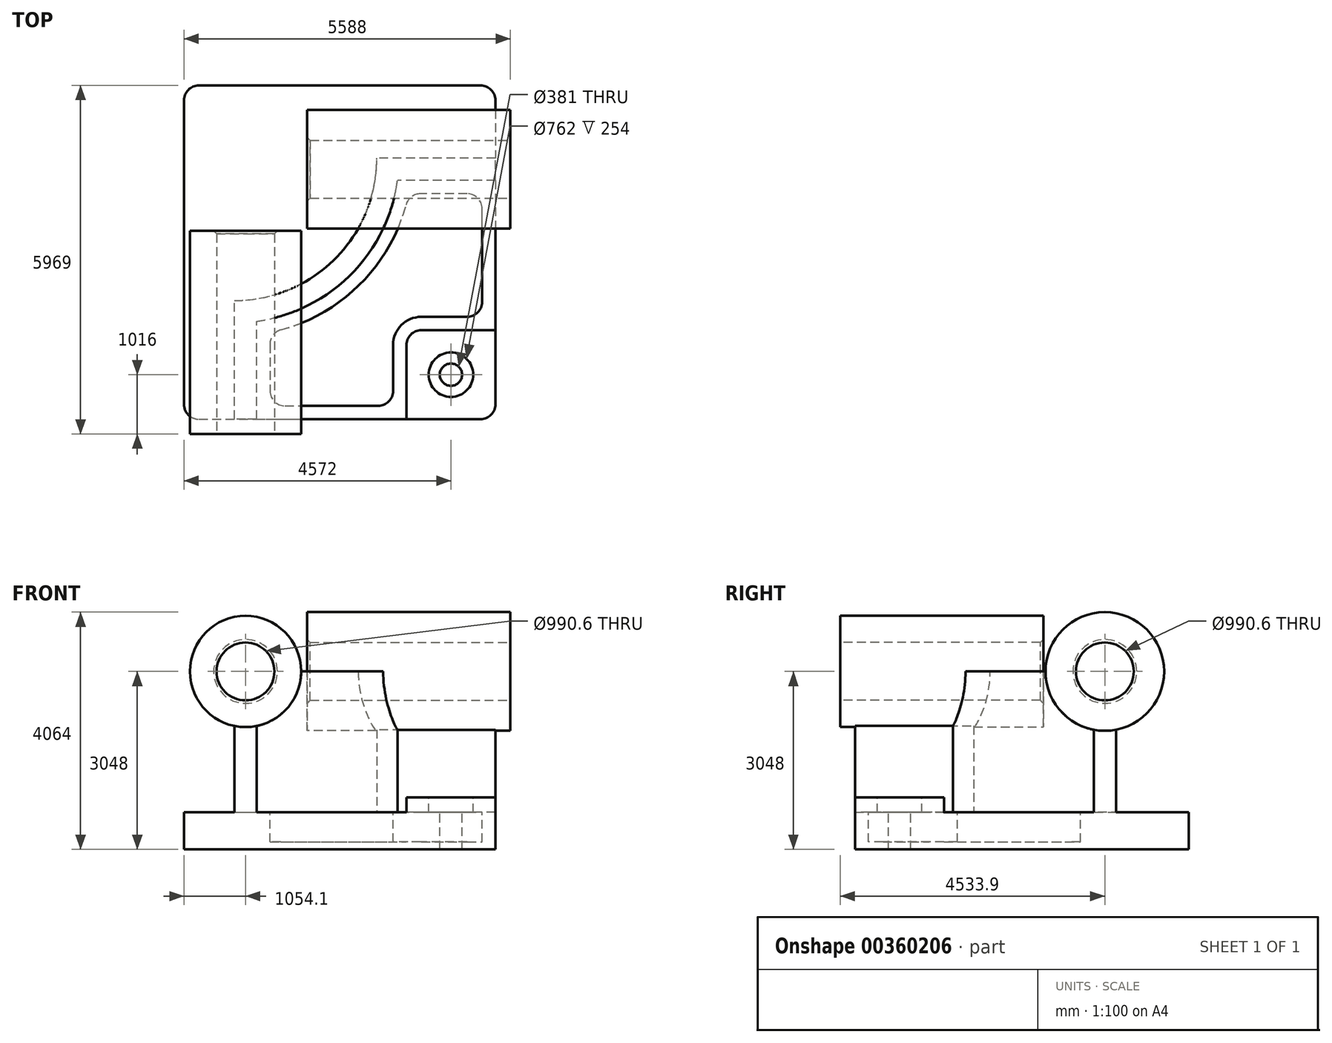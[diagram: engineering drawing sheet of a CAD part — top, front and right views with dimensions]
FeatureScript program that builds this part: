
annotation { "Feature Type Name" : "Feature", "Feature Type Description" : "" }
export const myFeature = defineFeature(function(context is Context, id is Id, definition is map)
    precondition{}
    {
        {
            var Q0;
            Q0=qCreatedBy(makeId("Top.planeOp"),FACE);
            var sketch = newSketch(context, id + "F0", { "sketchPlane" : qUnion([Q0])});
            skLineSegment(sketch, "E0.bottom", {"start": v(-2667, 2857.5) * mm, "end": v(2667, 2857.5) * mm});
            skLineSegment(sketch, "E0.top", {"start": v(-2667, -2857.5) * mm, "end": v(2667, -2857.5) * mm});
            skLineSegment(sketch, "E0.left", {"start": v(-2667, 2857.5) * mm, "end": v(-2667, -2857.5) * mm});
            skLineSegment(sketch, "E0.right", {"start": v(2667, 2857.5) * mm, "end": v(2667, -2857.5) * mm});
            skPoint(sketch, "E0.middle", {"position": v(0, 0) * mm});
            skSolve(sketch);
        }
        {
            var Q0;
            Q0=makeQuery(id+"F0.imprint","IMPRINT",FACE,{"disambiguationData":[TD([[makeQuery(id+"F0.imprint","IMPRINT",EDGE,{"derivedFrom":sQuery(id+"F0.wireOp",EDGE,"E0.bottom")}),-1.0]])]});
            extrude(context, id + "F1", {"entities" : qUnion([Q0]), "depth" : 635 * mm});
        }
        {
            var Q0;
            Q0=makeQuery(id+"F1.opExtrude","CAP_FACE",FACE,{"disambiguationData":[OSD([sQuery(id+"F0.wireOp",EDGE,"E0.bottom"),sQuery(id+"F0.wireOp",EDGE,"E0.top"),sQuery(id+"F0.wireOp",EDGE,"E0.left"),sQuery(id+"F0.wireOp",EDGE,"E0.right")])],"isStart":false});
            var sketch = newSketch(context, id + "F2", { "sketchPlane" : qUnion([Q0])});
            skLineSegment(sketch, "E1", {"start": v(-1803.4, -2857.5) * mm, "end": v(-1803.4, -825.5) * mm});
            skLineSegment(sketch, "E2", {"start": v(2667, 1612.9) * mm, "end": v(635, 1612.9) * mm});
            skArc(sketch, "E3", {"start": v(-1803.4, -825.5) * mm, "mid": v(-79.2, -111.3) * mm, "end": v(635, 1612.9) * mm});
            skLineSegment(sketch, "E4", {"start": v(-1803.4, 1612.9) * mm, "end": v(635, 1612.9) * mm, "construction": true});
            skLineSegment(sketch, "E5", {"start": v(-1803.4, 1612.9) * mm, "end": v(-1803.4, -825.5) * mm, "construction": true});
            skLineSegment(sketch, "E6.0", {"start": v(-1422.4, -2857.5) * mm, "end": v(-1422.4, -1180.64) * mm});
            skArc(sketch, "E6.1", {"start": v(-1422.4, -1180.64) * mm, "mid": v(190.22, -380.72) * mm, "end": v(990.14, 1231.9) * mm});
            skLineSegment(sketch, "E6.2", {"start": v(2667, 1231.9) * mm, "end": v(990.14, 1231.9) * mm});
            skLineSegment(sketch, "E7.0", {"start": v(2667, 2857.5) * mm, "end": v(2667, -2857.5) * mm});
            skLineSegment(sketch, "E8.0", {"start": v(-2667, -2857.5) * mm, "end": v(2667, -2857.5) * mm});
            skSolve(sketch);
        }
        {
            var Q0;
            {var subQ2=sQuery(id+"F2.wireOp",EDGE,"E1");Q0=makeQuery(id+"F2.imprint","IMPRINT",FACE,{"disambiguationData":[TD([[makeQuery(id+"F2.imprint","IMPRINT",EDGE,{"derivedFrom":subQ2}),-1.0]])]});}
            extrude(context, id + "F3", {"entities" : qUnion([Q0]), "operationType" : NewBodyOperationType.ADD, "depth" : 2413 * mm});
        }
        {
            var Q0;
            Q0=makeQuery(id+"F3.boolean.opBoolean","MERGE",FACE,{"derivedFrom":[makeQuery(id+"F1.opExtrude","SWEPT_FACE",FACE,{"disambiguationData":[OSD([sQuery(id+"F0.wireOp",EDGE,"E0.top")])]}),makeQuery(id+"F3.opExtrude","SWEPT_FACE",FACE,{"disambiguationData":[OSD([sQuery(id+"F2.wireOp",EDGE,"E8.0")])]})]});
            var sketch = newSketch(context, id + "F4", { "sketchPlane" : qUnion([Q0])});
            skCircle(sketch, "E9", {"center": v(-1612.9, 3048) * mm, "radius": 952.5 * mm});
            skSolve(sketch);
        }
        {
            var Q0;
            Q0 = qSketchRegion(id + "F4", true);
            extrude(context, id + "F5", {"entities" : qUnion([Q0]), "operationType" : NewBodyOperationType.ADD, "depth" : 254 * mm, "hasSecondDirection" : true, "secondDirectionOppositeDirection" : true, "secondDirectionDepth" : 3225.8 * mm});
        }
        {
            var Q0;
            Q0=makeQuery(id+"F3.boolean.opBoolean","MERGE",FACE,{"derivedFrom":[makeQuery(id+"F1.opExtrude","SWEPT_FACE",FACE,{"disambiguationData":[OSD([sQuery(id+"F0.wireOp",EDGE,"E0.right")])]}),makeQuery(id+"F3.opExtrude","SWEPT_FACE",FACE,{"disambiguationData":[OSD([sQuery(id+"F2.wireOp",EDGE,"E7.0")])]})]});
            var sketch = newSketch(context, id + "F6", { "sketchPlane" : qUnion([Q0])});
            skCircle(sketch, "E10", {"center": v(1422.4, 3048) * mm, "radius": 1016 * mm});
            skSolve(sketch);
        }
        {
            var Q0;
            Q0 = qSketchRegion(id + "F6", true);
            extrude(context, id + "F7", {"entities" : qUnion([Q0]), "operationType" : NewBodyOperationType.ADD, "depth" : 254 * mm, "hasSecondDirection" : true, "secondDirectionOppositeDirection" : true, "secondDirectionDepth" : 3225.8 * mm});
        }
        {
            var Q0;
            {var subQ0=sQuery(id+"F0.wireOp",EDGE,"E0.right");var subQ1=sQuery(id+"F0.wireOp",EDGE,"E0.top");Q0=makeQuery(id+"F3.boolean.opBoolean","SPLIT",FACE,{"disambiguationData":[TD([makeQuery(id+"F3.opExtrude","SWEPT_FACE",FACE,{"disambiguationData":[OSD([sQuery(id+"F2.wireOp",EDGE,"E6.0")])]})])],"derivedFrom":makeQuery(id+"F1.opExtrude","CAP_FACE",FACE,{"disambiguationData":[OSD([sQuery(id+"F0.wireOp",EDGE,"E0.bottom"),subQ1,sQuery(id+"F0.wireOp",EDGE,"E0.left"),subQ0])],"isStart":false})});}
            var sketch = newSketch(context, id + "F8", { "sketchPlane" : qUnion([Q0])});
            skLineSegment(sketch, "E11.bottom", {"start": v(2667, -2857.5) * mm, "end": v(1143, -2857.5) * mm});
            skLineSegment(sketch, "E11.top", {"start": v(2667, -1333.5) * mm, "end": v(1143, -1333.5) * mm});
            skLineSegment(sketch, "E11.left", {"start": v(2667, -2857.5) * mm, "end": v(2667, -1333.5) * mm});
            skLineSegment(sketch, "E11.right", {"start": v(1143, -2857.5) * mm, "end": v(1143, -1333.5) * mm});
            skSolve(sketch);
        }
        {
            var Q0;
            Q0=makeQuery(id+"F8.imprint","IMPRINT",FACE,{"disambiguationData":[TD([[makeQuery(id+"F8.imprint","IMPRINT",EDGE,{"derivedFrom":sQuery(id+"F8.wireOp",EDGE,"E11.bottom")}),1.0]])]});
            extrude(context, id + "F9", {"entities" : qUnion([Q0]), "operationType" : NewBodyOperationType.ADD, "depth" : 254 * mm});
        }
        {
            var Q0;
            Q0=makeQuery(id+"F9.opExtrude","SWEPT_EDGE",EDGE,{"disambiguationData":[OSD([sQuery(id+"F8.wireOp",EDGE,"E11.top"),sQuery(id+"F8.wireOp",EDGE,"E11.right")])]});
            fillet(context, id + "F10", {"entities" : qUnion([Q0]), "radius" : 254 * mm, "tangentPropagation" : true, "allowEdgeOverflow" : false});
        }
        {
            var Q0;
            {var subQ0=sQuery(id+"F0.wireOp",EDGE,"E0.right");var subQ1=sQuery(id+"F0.wireOp",EDGE,"E0.top");Q0=makeQuery(id+"F3.boolean.opBoolean","SPLIT",FACE,{"disambiguationData":[TD([makeQuery(id+"F3.opExtrude","SWEPT_FACE",FACE,{"disambiguationData":[OSD([sQuery(id+"F2.wireOp",EDGE,"E6.0")])]})])],"derivedFrom":makeQuery(id+"F1.opExtrude","CAP_FACE",FACE,{"disambiguationData":[OSD([sQuery(id+"F0.wireOp",EDGE,"E0.bottom"),subQ1,sQuery(id+"F0.wireOp",EDGE,"E0.left"),subQ0])],"isStart":false})});}
            var sketch = newSketch(context, id + "F11", { "sketchPlane" : qUnion([Q0])});
            skLineSegment(sketch, "E12.0", {"start": v(-1193.8, -1373.52) * mm, "end": v(-1193.8, -2628.9) * mm});
            skArc(sketch, "E12.1", {"start": v(1183.02, 1003.3) * mm, "mid": v(351.86, -542.36) * mm, "end": v(-1193.8, -1373.52) * mm});
            skLineSegment(sketch, "E12.2", {"start": v(-1193.8, -2628.9) * mm, "end": v(914.4, -2628.9) * mm});
            skLineSegment(sketch, "E12.3", {"start": v(2438.4, 1003.3) * mm, "end": v(1183.02, 1003.3) * mm});
            skLineSegment(sketch, "E12.4", {"start": v(914.4, -2628.9) * mm, "end": v(914.4, -1587.5) * mm});
            skArc(sketch, "E12.5", {"start": v(914.4, -1587.5) * mm, "mid": v(1055.75, -1246.25) * mm, "end": v(1397, -1104.9) * mm});
            skLineSegment(sketch, "E12.6", {"start": v(1397, -1104.9) * mm, "end": v(2438.4, -1104.9) * mm});
            skLineSegment(sketch, "E12.7", {"start": v(2438.4, -1104.9) * mm, "end": v(2438.4, 1003.3) * mm});
            skLineSegment(sketch, "E13.0", {"start": v(-1428.75, -1175.09) * mm, "end": v(-1428.75, -2863.85) * mm});
            skArc(sketch, "E13.1", {"start": v(984.59, 1238.25) * mm, "mid": v(185.73, -376.23) * mm, "end": v(-1428.75, -1175.09) * mm});
            skLineSegment(sketch, "E13.2", {"start": v(-1428.75, -2863.85) * mm, "end": v(1149.35, -2863.85) * mm});
            skLineSegment(sketch, "E13.3", {"start": v(2673.35, 1238.25) * mm, "end": v(984.59, 1238.25) * mm});
            skLineSegment(sketch, "E13.4", {"start": v(1149.35, -2863.85) * mm, "end": v(1149.35, -1587.5) * mm});
            skArc(sketch, "E13.5", {"start": v(1149.35, -1587.5) * mm, "mid": v(1221.89, -1412.39) * mm, "end": v(1397, -1339.85) * mm});
            skLineSegment(sketch, "E13.6", {"start": v(1397, -1339.85) * mm, "end": v(2673.35, -1339.85) * mm});
            skLineSegment(sketch, "E13.7", {"start": v(2673.35, -1339.85) * mm, "end": v(2673.35, 1238.25) * mm});
            skSolve(sketch);
        }
        {
            var Q0;
            Q0=makeQuery(id+"F11.imprint","IMPRINT",FACE,{"disambiguationData":[TD([[makeQuery(id+"F11.imprint","IMPRINT",EDGE,{"derivedFrom":sQuery(id+"F11.wireOp",EDGE,"E12.0")}),1.0]])]});
            extrude(context, id + "F12", {"entities" : qUnion([Q0]), "operationType" : NewBodyOperationType.REMOVE, "oppositeDirection" : true, "depth" : 508 * mm});
        }
        {
            var Q0;
            Q0=makeQuery(id+"F9.opExtrude","CAP_FACE",FACE,{"disambiguationData":[OSD([sQuery(id+"F8.wireOp",EDGE,"E11.bottom"),sQuery(id+"F8.wireOp",EDGE,"E11.top"),sQuery(id+"F8.wireOp",EDGE,"E11.left"),sQuery(id+"F8.wireOp",EDGE,"E11.right")])],"isStart":false});
            var sketch = newSketch(context, id + "F13", { "sketchPlane" : qUnion([Q0])});
            skCircle(sketch, "E14", {"center": v(1905, -2095.5) * mm, "radius": 381 * mm});
            skSolve(sketch);
        }
        {
            var Q0;
            Q0=sQuery(id+"F13.wireOp",VERTEX,"E14.center");
            var Q1;
            Q1=makeQuery(id+"F1.opExtrude","SWEPT_BODY",BODY,{"disambiguationData":[OSD([sQuery(id+"F0.wireOp",EDGE,"E0.bottom"),sQuery(id+"F0.wireOp",EDGE,"E0.top"),sQuery(id+"F0.wireOp",EDGE,"E0.left"),sQuery(id+"F0.wireOp",EDGE,"E0.right")])]});
            hole(context, id + "F14", {"style" : HoleStyle.C_BORE, "endStyle" : HoleEndStyle.THROUGH, "holeDiameter" : 381 * mm, "cBoreDiameter" : 762 * mm, "cBoreDepth" : 254 * mm, "isTappedThrough" : true, "tappedDepth" : 12.7 * mm, "tapClearance" : 3, "locations" : qUnion([Q0]), "scope" : qUnion([Q1])});
        }
        {
            var Q0;
            Q0=makeQuery(id+"F12.boolean.opBoolean","COPY",EDGE,{"derivedFrom":makeQuery(id+"F12.opExtrude","SWEPT_EDGE",EDGE,{"disambiguationData":[OSD([sQuery(id+"F11.wireOp",EDGE,"E12.0"),sQuery(id+"F11.wireOp",EDGE,"E12.1")])]})});
            var Q1;
            Q1=makeQuery(id+"F12.boolean.opBoolean","COPY",EDGE,{"derivedFrom":makeQuery(id+"F12.opExtrude","SWEPT_EDGE",EDGE,{"disambiguationData":[OSD([sQuery(id+"F11.wireOp",EDGE,"E12.1"),sQuery(id+"F11.wireOp",EDGE,"E12.3")])]})});
            var Q2;
            Q2=makeQuery(id+"F12.boolean.opBoolean","COPY",EDGE,{"derivedFrom":makeQuery(id+"F12.opExtrude","SWEPT_EDGE",EDGE,{"disambiguationData":[OSD([sQuery(id+"F11.wireOp",EDGE,"E12.0"),sQuery(id+"F11.wireOp",EDGE,"E12.2")])]})});
            var Q3;
            Q3=makeQuery(id+"F12.boolean.opBoolean","COPY",EDGE,{"derivedFrom":makeQuery(id+"F12.opExtrude","SWEPT_EDGE",EDGE,{"disambiguationData":[OSD([sQuery(id+"F11.wireOp",EDGE,"E12.3"),sQuery(id+"F11.wireOp",EDGE,"E12.7")])]})});
            var Q4;
            Q4=makeQuery(id+"F12.boolean.opBoolean","COPY",EDGE,{"derivedFrom":makeQuery(id+"F12.opExtrude","SWEPT_EDGE",EDGE,{"disambiguationData":[OSD([sQuery(id+"F11.wireOp",EDGE,"E12.2"),sQuery(id+"F11.wireOp",EDGE,"E12.4")])]})});
            var Q5;
            Q5=makeQuery(id+"F12.boolean.opBoolean","COPY",EDGE,{"derivedFrom":makeQuery(id+"F12.opExtrude","SWEPT_EDGE",EDGE,{"disambiguationData":[OSD([sQuery(id+"F11.wireOp",EDGE,"E12.6"),sQuery(id+"F11.wireOp",EDGE,"E12.7")])]})});
            fillet(context, id + "F15", {"entities" : qUnion([Q0, Q1, Q2, Q3, Q4, Q5]), "radius" : 254 * mm, "tangentPropagation" : true, "allowEdgeOverflow" : false});
        }
        {
            var Q0;
            Q0=makeQuery(id+"F5.opExtrude","CAP_FACE",FACE,{"disambiguationData":[OSD([sQuery(id+"F4.wireOp",EDGE,"E9")])],"isStart":false});
            var sketch = newSketch(context, id + "F16", { "sketchPlane" : qUnion([Q0])});
            skCircle(sketch, "E15", {"center": v(-1612.9, 3048) * mm, "radius": 495.3 * mm});
            skSolve(sketch);
        }
        {
            var Q0;
            Q0 = qSketchRegion(id + "F16", true);
            extrude(context, id + "F17", {"entities" : qUnion([Q0]), "operationType" : NewBodyOperationType.REMOVE, "endBound" : BoundingType.THROUGH_ALL, "oppositeDirection" : true, "depth" : 25.4 * mm});
        }
        {
            var Q0;
            Q0=makeQuery(id+"F7.opExtrude","CAP_FACE",FACE,{"disambiguationData":[OSD([sQuery(id+"F6.wireOp",EDGE,"E10")])],"isStart":false});
            var sketch = newSketch(context, id + "F18", { "sketchPlane" : qUnion([Q0])});
            skCircle(sketch, "E16", {"center": v(1422.4, 3048) * mm, "radius": 495.3 * mm});
            skSolve(sketch);
        }
        {
            var Q0;
            Q0 = qSketchRegion(id + "F18", true);
            extrude(context, id + "F19", {"entities" : qUnion([Q0]), "operationType" : NewBodyOperationType.REMOVE, "endBound" : BoundingType.THROUGH_ALL, "oppositeDirection" : true, "depth" : 25.4 * mm});
        }
        {
            var Q0;
            Q0=makeQuery(id+"F17.boolean.opBoolean","COPY",EDGE,{"derivedFrom":makeQuery(id+"F17.opExtrude","CAP_EDGE",EDGE,{"disambiguationData":[OSD([sQuery(id+"F16.wireOp",EDGE,"E15")])],"isStart":true})});
            var Q1;
            Q1=makeQuery(id+"F19.boolean.opBoolean","COPY",EDGE,{"derivedFrom":makeQuery(id+"F19.opExtrude","CAP_EDGE",EDGE,{"disambiguationData":[OSD([sQuery(id+"F18.wireOp",EDGE,"E16")])],"isStart":true})});
            var Q2;
            Q2=makeQuery(id+"F17.boolean.opBoolean","INTERSECT",EDGE,{"derivedFrom":[makeQuery(id+"F5.opExtrude","CAP_FACE",FACE,{"disambiguationData":[OSD([sQuery(id+"F4.wireOp",EDGE,"E9")])],"isStart":true}),makeQuery(id+"F17.opExtrude","SWEPT_FACE",FACE,{"disambiguationData":[OSD([sQuery(id+"F16.wireOp",EDGE,"E15")])]})]});
            var Q3;
            Q3=makeQuery(id+"F19.boolean.opBoolean","INTERSECT",EDGE,{"derivedFrom":[makeQuery(id+"F7.opExtrude","CAP_FACE",FACE,{"disambiguationData":[OSD([sQuery(id+"F6.wireOp",EDGE,"E10")])],"isStart":true}),makeQuery(id+"F19.opExtrude","SWEPT_FACE",FACE,{"disambiguationData":[OSD([sQuery(id+"F18.wireOp",EDGE,"E16")])]})]});
            chamfer(context, id + "F20", {"entities" : qUnion([Q0, Q1, Q2, Q3]), "width" : 50.8 * mm, "tangentPropagation" : true});
        }
        {
            var Q0;
            Q0=makeQuery(id+"F9.boolean.opBoolean","MERGE",EDGE,{"derivedFrom":[makeQuery(id+"F1.opExtrude","SWEPT_EDGE",EDGE,{"disambiguationData":[OSD([sQuery(id+"F0.wireOp",EDGE,"E0.top"),sQuery(id+"F0.wireOp",EDGE,"E0.right")])]}),makeQuery(id+"F9.opExtrude","SWEPT_EDGE",EDGE,{"disambiguationData":[OSD([sQuery(id+"F8.wireOp",EDGE,"E11.bottom"),sQuery(id+"F8.wireOp",EDGE,"E11.left")])]})]});
            var Q1;
            Q1=makeQuery(id+"F1.opExtrude","SWEPT_EDGE",EDGE,{"disambiguationData":[OSD([sQuery(id+"F0.wireOp",EDGE,"E0.bottom"),sQuery(id+"F0.wireOp",EDGE,"E0.right")])]});
            var Q2;
            Q2=makeQuery(id+"F1.opExtrude","SWEPT_EDGE",EDGE,{"disambiguationData":[OSD([sQuery(id+"F0.wireOp",EDGE,"E0.top"),sQuery(id+"F0.wireOp",EDGE,"E0.left")])]});
            var Q3;
            Q3=makeQuery(id+"F1.opExtrude","SWEPT_EDGE",EDGE,{"disambiguationData":[OSD([sQuery(id+"F0.wireOp",EDGE,"E0.bottom"),sQuery(id+"F0.wireOp",EDGE,"E0.left")])]});
            fillet(context, id + "F21", {"entities" : qUnion([Q0, Q1, Q2, Q3]), "radius" : 254 * mm, "tangentPropagation" : true, "allowEdgeOverflow" : false});
        }
    });
